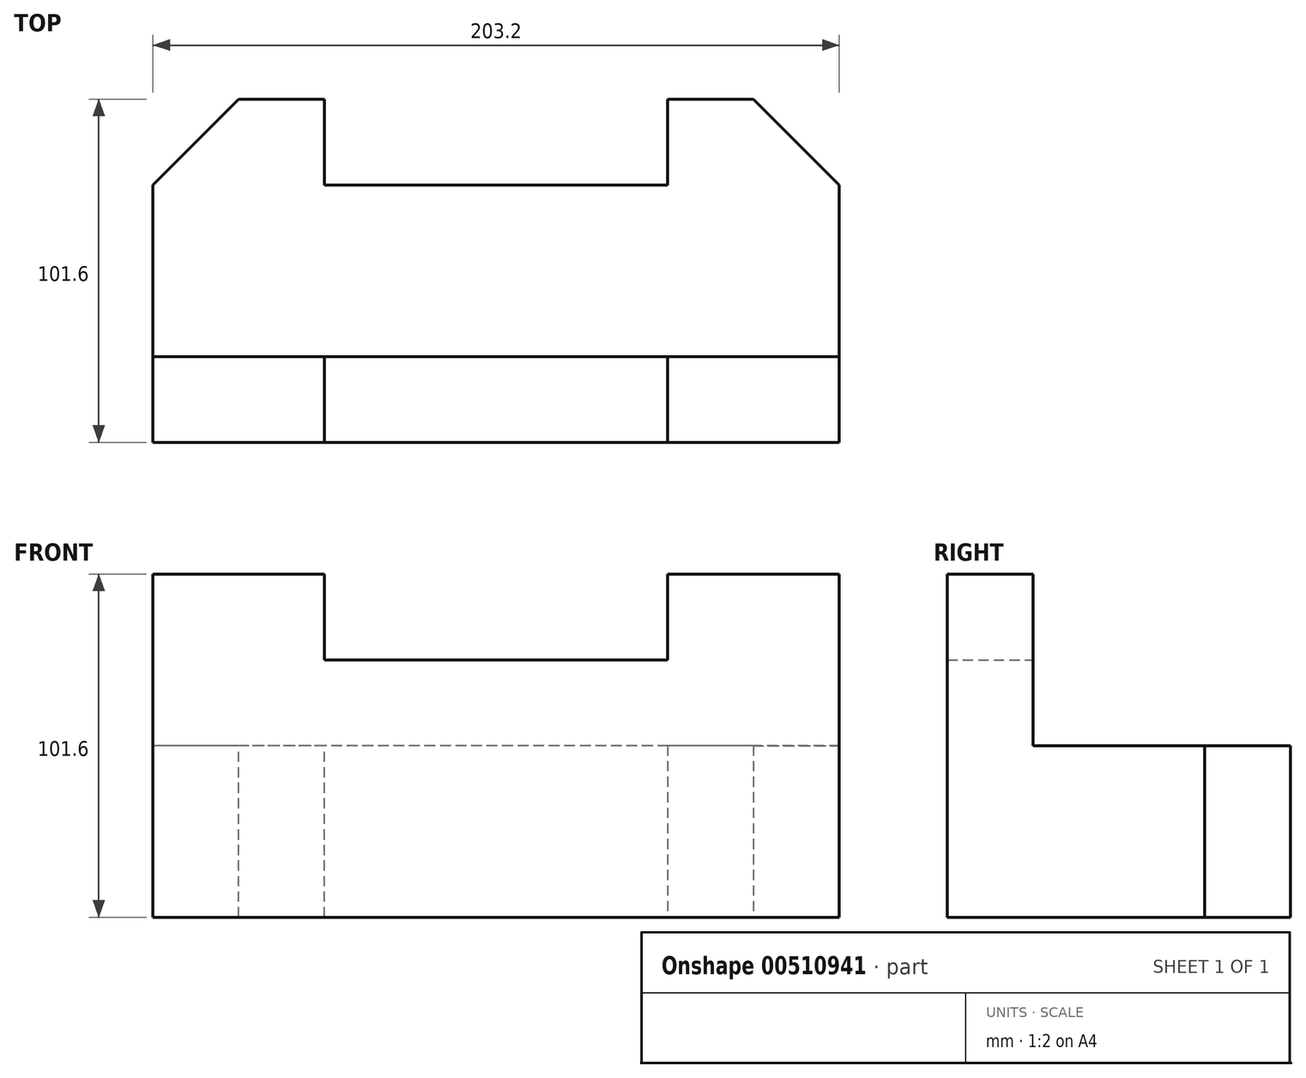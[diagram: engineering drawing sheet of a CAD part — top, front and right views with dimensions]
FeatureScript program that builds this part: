
annotation { "Feature Type Name" : "Feature", "Feature Type Description" : "" }
export const myFeature = defineFeature(function(context is Context, id is Id, definition is map)
    precondition{}
    {
        {
            var Q0;
            Q0=qCreatedBy(makeId("Right.planeOp"),FACE);
            var sketch = newSketch(context, id + "F0", { "sketchPlane" : qUnion([Q0])});
            skLineSegment(sketch, "E0.bottom", {"start": v(0, 0) * mm, "end": v(-76.2, 0) * mm});
            skLineSegment(sketch, "E0.top", {"start": v(0, 50.8) * mm, "end": v(-76.2, 50.8) * mm});
            skLineSegment(sketch, "E0.left", {"start": v(0, 0) * mm, "end": v(0, 50.8) * mm});
            skLineSegment(sketch, "E0.right", {"start": v(-76.2, 0) * mm, "end": v(-76.2, 50.8) * mm});
            skSolve(sketch);
        }
        {
            var Q0;
            Q0 = qSketchRegion(id + "F0", true);
            extrude(context, id + "F1", {"entities" : qUnion([Q0]), "depth" : 203.2 * mm});
        }
        {
            var Q0;
            Q0=makeQuery(id+"F1.opExtrude","SWEPT_FACE",FACE,{"disambiguationData":[OSD([sQuery(id+"F0.wireOp",EDGE,"E0.top")])]});
            var sketch = newSketch(context, id + "F2", { "sketchPlane" : qUnion([Q0])});
            skLineSegment(sketch, "E1.bottom", {"start": v(203.2, -76.2) * mm, "end": v(0, -76.2) * mm});
            skLineSegment(sketch, "E1.top", {"start": v(203.2, -50.8) * mm, "end": v(0, -50.8) * mm});
            skLineSegment(sketch, "E1.left", {"start": v(203.2, -76.2) * mm, "end": v(203.2, -50.8) * mm});
            skLineSegment(sketch, "E1.right", {"start": v(0, -76.2) * mm, "end": v(0, -50.8) * mm});
            skSolve(sketch);
        }
        {
            var Q0;
            Q0 = qSketchRegion(id + "F2", true);
            extrude(context, id + "F3", {"entities" : qUnion([Q0]), "operationType" : NewBodyOperationType.ADD, "depth" : 50.8 * mm});
        }
        {
            var Q0;
            Q0=makeQuery(id+"F3.opExtrude","SWEPT_FACE",FACE,{"disambiguationData":[OSD([sQuery(id+"F2.wireOp",EDGE,"E1.top")])]});
            var sketch = newSketch(context, id + "F4", { "sketchPlane" : qUnion([Q0])});
            skLineSegment(sketch, "E2.bottom", {"start": v(-50.8, 101.6) * mm, "end": v(-152.4, 101.6) * mm});
            skLineSegment(sketch, "E2.top", {"start": v(-50.8, 76.2) * mm, "end": v(-152.4, 76.2) * mm});
            skLineSegment(sketch, "E2.left", {"start": v(-50.8, 101.6) * mm, "end": v(-50.8, 76.2) * mm});
            skLineSegment(sketch, "E2.right", {"start": v(-152.4, 101.6) * mm, "end": v(-152.4, 76.2) * mm});
            skSolve(sketch);
        }
        {
            var Q0;
            Q0=makeQuery(id+"F4.imprint","IMPRINT",FACE,{"disambiguationData":[TD([[makeQuery(id+"F4.imprint","IMPRINT",EDGE,{"derivedFrom":sQuery(id+"F4.wireOp",EDGE,"E2.bottom")}),-1.0]])]});
            extrude(context, id + "F5", {"entities" : qUnion([Q0]), "operationType" : NewBodyOperationType.REMOVE, "oppositeDirection" : true, "depth" : 25.4 * mm});
        }
        {
            var Q0;
            Q0=makeQuery(id+"F1.opExtrude","SWEPT_FACE",FACE,{"disambiguationData":[OSD([sQuery(id+"F0.wireOp",EDGE,"E0.left")])]});
            var sketch = newSketch(context, id + "F6", { "sketchPlane" : qUnion([Q0])});
            skLineSegment(sketch, "E3.bottom", {"start": v(-152.4, 50.8) * mm, "end": v(-177.8, 50.8) * mm});
            skLineSegment(sketch, "E3.top", {"start": v(-152.4, 0) * mm, "end": v(-177.8, 0) * mm});
            skLineSegment(sketch, "E3.left", {"start": v(-152.4, 50.8) * mm, "end": v(-152.4, 0) * mm});
            skLineSegment(sketch, "E3.right", {"start": v(-177.8, 50.8) * mm, "end": v(-177.8, 0) * mm});
            skSolve(sketch);
        }
        {
            var Q0;
            Q0 = qSketchRegion(id + "F6", true);
            extrude(context, id + "F7", {"entities" : qUnion([Q0]), "operationType" : NewBodyOperationType.ADD, "depth" : 25.4 * mm});
        }
        {
            var Q0;
            {var subQ1=sQuery(id+"F0.wireOp",EDGE,"E0.left");Q0=makeQuery(id+"F7.boolean.opBoolean","SPLIT",FACE,{"disambiguationData":[TD([makeQuery(id+"F3.opExtrude","SWEPT_FACE",FACE,{"disambiguationData":[OSD([sQuery(id+"F2.wireOp",EDGE,"E1.right")])]})])],"derivedFrom":makeQuery(id+"F1.opExtrude","SWEPT_FACE",FACE,{"disambiguationData":[OSD([subQ1])]})});}
            var sketch = newSketch(context, id + "F8", { "sketchPlane" : qUnion([Q0])});
            skLineSegment(sketch, "E4.bottom", {"start": v(-50.8, 0) * mm, "end": v(-25.4, 0) * mm});
            skLineSegment(sketch, "E4.top", {"start": v(-50.8, 50.8) * mm, "end": v(-25.4, 50.8) * mm});
            skLineSegment(sketch, "E4.left", {"start": v(-50.8, 0) * mm, "end": v(-50.8, 50.8) * mm});
            skLineSegment(sketch, "E4.right", {"start": v(-25.4, 0) * mm, "end": v(-25.4, 50.8) * mm});
            skSolve(sketch);
        }
        {
            var Q0;
            Q0 = qSketchRegion(id + "F8", true);
            extrude(context, id + "F9", {"entities" : qUnion([Q0]), "operationType" : NewBodyOperationType.ADD, "depth" : 25.4 * mm});
        }
        {
            var Q0;
            Q0=makeQuery(id+"F9.boolean.opBoolean","MERGE",FACE,{"derivedFrom":[makeQuery(id+"F7.boolean.opBoolean","MERGE",FACE,{"derivedFrom":[makeQuery(id+"F1.opExtrude","SWEPT_FACE",FACE,{"disambiguationData":[OSD([sQuery(id+"F0.wireOp",EDGE,"E0.bottom")])]}),makeQuery(id+"F7.opExtrude","SWEPT_FACE",FACE,{"disambiguationData":[OSD([sQuery(id+"F6.wireOp",EDGE,"E3.top")])]})]}),makeQuery(id+"F9.opExtrude","SWEPT_FACE",FACE,{"disambiguationData":[OSD([sQuery(id+"F8.wireOp",EDGE,"E4.bottom")])]})]});
            var sketch = newSketch(context, id + "F10", { "sketchPlane" : qUnion([Q0])});
            skLineSegment(sketch, "E5", {"start": v(177.8, -25.4) * mm, "end": v(203.2, 0) * mm});
            skSolve(sketch);
        }
        {
            var Q0;
            Q0=makeQuery(id+"F10.imprint","IMPRINT",FACE,{"disambiguationData":[TD([[makeQuery(id+"F10.imprint","IMPRINT",EDGE,{"derivedFrom":sQuery(id+"F10.wireOp",EDGE,"E5")}),1.0]])]});
            extrude(context, id + "F11", {"entities" : qUnion([Q0]), "operationType" : NewBodyOperationType.ADD, "oppositeDirection" : true, "depth" : 50.8 * mm});
        }
        {
            var Q0;
            {var subQ0=sQuery(id+"F6.wireOp",EDGE,"E3.top");var subQ1=sQuery(id+"F0.wireOp",EDGE,"E0.bottom");Q0=makeQuery(id+"F11.boolean.opBoolean","MERGE",FACE,{"derivedFrom":[makeQuery(id+"F9.boolean.opBoolean","MERGE",FACE,{"derivedFrom":[makeQuery(id+"F7.boolean.opBoolean","MERGE",FACE,{"derivedFrom":[makeQuery(id+"F1.opExtrude","SWEPT_FACE",FACE,{"disambiguationData":[OSD([subQ1])]}),makeQuery(id+"F7.opExtrude","SWEPT_FACE",FACE,{"disambiguationData":[OSD([subQ0])]})]}),makeQuery(id+"F9.opExtrude","SWEPT_FACE",FACE,{"disambiguationData":[OSD([sQuery(id+"F8.wireOp",EDGE,"E4.bottom")])]})]}),makeQuery(id+"F11.opExtrude","CAP_FACE",FACE,{"disambiguationData":[OSD([subQ1,sQuery(id+"F0.wireOp",EDGE,"E0.left"),subQ0,sQuery(id+"F6.wireOp",EDGE,"E3.right"),sQuery(id+"F10.wireOp",EDGE,"E5")])],"isStart":true})]});}
            var sketch = newSketch(context, id + "F12", { "sketchPlane" : qUnion([Q0])});
            skLineSegment(sketch, "E6", {"start": v(25.4, -25.4) * mm, "end": v(0, 0) * mm});
            skSolve(sketch);
        }
        {
            var Q0;
            Q0=makeQuery(id+"F12.imprint","IMPRINT",FACE,{"disambiguationData":[TD([[makeQuery(id+"F12.imprint","IMPRINT",EDGE,{"derivedFrom":sQuery(id+"F12.wireOp",EDGE,"E6")}),-1.0]])]});
            extrude(context, id + "F13", {"entities" : qUnion([Q0]), "operationType" : NewBodyOperationType.ADD, "oppositeDirection" : true, "depth" : 50.8 * mm});
        }
    });
